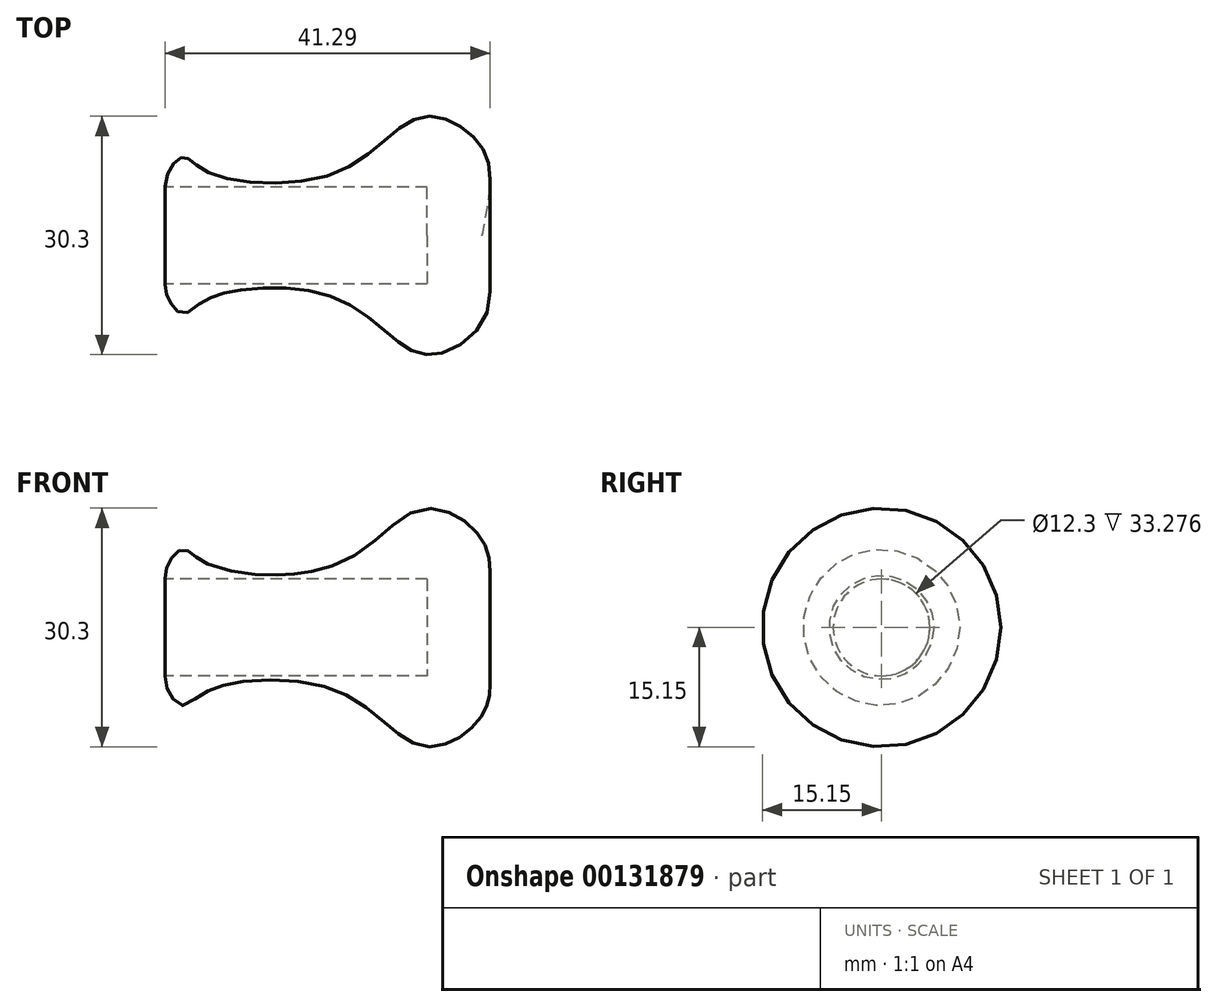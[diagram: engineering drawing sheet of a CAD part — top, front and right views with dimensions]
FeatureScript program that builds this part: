
annotation { "Feature Type Name" : "Feature", "Feature Type Description" : "" }
export const myFeature = defineFeature(function(context is Context, id is Id, definition is map)
    precondition{}
    {
        {
            var Q0;
            Q0=qCreatedBy(makeId("Top.planeOp"),FACE);
            var sketch = newSketch(context, id + "F0", { "sketchPlane" : qUnion([Q0])});
            skFitSpline(sketch, "E0", {"points": [v(40, 0) * mm, v(39.55, 11.78) * mm, v(32.36, 15.06) * mm, v(21.97, 8.2) * mm, v(4.85, 8.21) * mm, v(1.96, 9.93) * mm, v(-0.19, 7.14) * mm, v(0, 0) * mm], "startDerivative": vector(23.55, 112.95) * mm, "endDerivative": vector(-12.56, -70.25) * mm});
            skLineSegment(sketch, "E1", {"start": v(-8.04, 0) * mm, "end": v(49.03, 0) * mm});
            skSolve(sketch);
        }
        {
            var Q0;
            Q0 = qSketchRegion(id + "F0", true);
            var Q1;
            Q1=sQuery(id+"F0.wireOp",EDGE,"E1");
            revolve(context, id + "F1", {"entities" : qUnion([Q0]), "axis" : qUnion([Q1]), "revolveType" : RevolveType.FULL});
        }
        {
            var Q0;
            Q0=qCreatedBy(makeId("Right.planeOp"),FACE);
            var sketch = newSketch(context, id + "F2", { "sketchPlane" : qUnion([Q0])});
            skCircle(sketch, "E2", {"center": v(0, 0) * mm, "radius": 6.15 * mm});
            skSolve(sketch);
        }
        {
            var Q0;
            Q0=makeQuery(id+"F2.imprint","IMPRINT",FACE,{"disambiguationData":[TD([[makeQuery(id+"F2.imprint","IMPRINT",EDGE,{"derivedFrom":sQuery(id+"F2.wireOp",EDGE,"E2")}),1.0]])]});
            extrude(context, id + "F3", {"entities" : qUnion([Q0]), "operationType" : NewBodyOperationType.REMOVE, "endBound" : BoundingType.SYMMETRIC, "depth" : 66 * mm});
        }
    });
